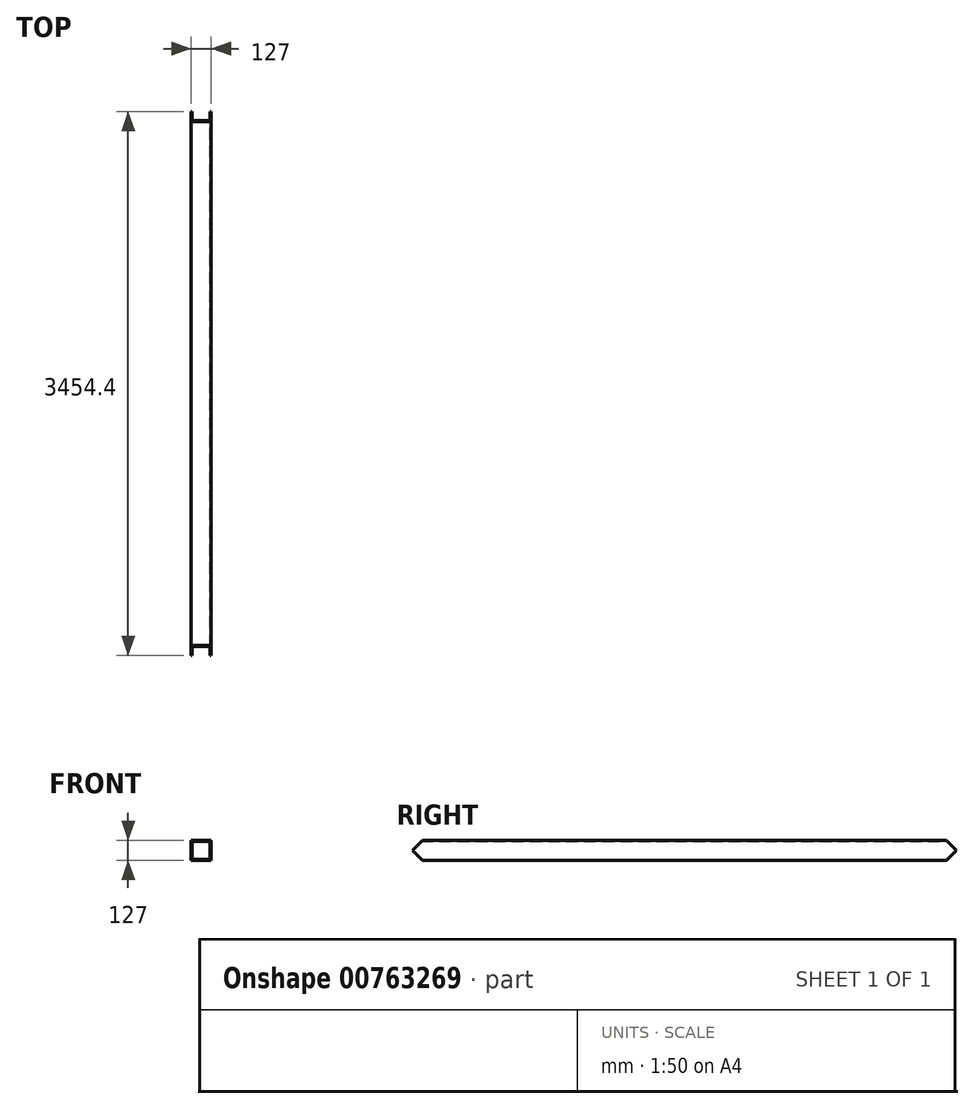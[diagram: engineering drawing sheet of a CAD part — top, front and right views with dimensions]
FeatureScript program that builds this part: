
annotation { "Feature Type Name" : "Feature", "Feature Type Description" : "" }
export const myFeature = defineFeature(function(context is Context, id is Id, definition is map)
    precondition{}
    {
        {
            var Q0;
            Q0=qCreatedBy(makeId("Front.planeOp"),FACE);
            var sketch = newSketch(context, id + "F0", { "sketchPlane" : qUnion([Q0])});
            skLineSegment(sketch, "E0.bottom", {"start": v(-63.5, 63.5) * mm, "end": v(63.5, 63.5) * mm});
            skLineSegment(sketch, "E0.top", {"start": v(-63.5, -63.5) * mm, "end": v(63.5, -63.5) * mm});
            skLineSegment(sketch, "E0.left", {"start": v(-63.5, 63.5) * mm, "end": v(-63.5, -63.5) * mm});
            skLineSegment(sketch, "E0.right", {"start": v(63.5, 63.5) * mm, "end": v(63.5, -63.5) * mm});
            skLineSegment(sketch, "E1.bottom", {"start": v(-57.15, 57.15) * mm, "end": v(57.15, 57.15) * mm});
            skLineSegment(sketch, "E1.top", {"start": v(-57.15, -57.15) * mm, "end": v(57.15, -57.15) * mm});
            skLineSegment(sketch, "E1.left", {"start": v(-57.15, 57.15) * mm, "end": v(-57.15, -57.15) * mm});
            skLineSegment(sketch, "E1.right", {"start": v(57.15, 57.15) * mm, "end": v(57.15, -57.15) * mm});
            skLineSegment(sketch, "E2", {"start": v(-57.15, 57.15) * mm, "end": v(57.15, -57.15) * mm, "construction": true});
            skLineSegment(sketch, "E3", {"start": v(63.5, 63.5) * mm, "end": v(-63.5, -63.5) * mm, "construction": true});
            skSolve(sketch);
        }
        {
            var Q0;
            Q0 = qSketchRegion(id + "F0", true);
            extrude(context, id + "F1", {"entities" : qUnion([Q0]), "endBound" : BoundingType.SYMMETRIC, "depth" : 3454.4 * mm, "offsetDistance" : 25.4 * mm});
        }
        {
            var Q0;
            Q0=makeQuery(id+"F1.opExtrude","SWEPT_FACE",FACE,{"disambiguationData":[OSD([sQuery(id+"F0.wireOp",EDGE,"E0.right")])]});
            var sketch = newSketch(context, id + "F2", { "sketchPlane" : qUnion([Q0])});
            skLineSegment(sketch, "E4", {"start": v(1727.2, 0) * mm, "end": v(1727.2, 63.5) * mm});
            skLineSegment(sketch, "E5", {"start": v(1727.2, 63.5) * mm, "end": v(1663.7, 63.5) * mm});
            skLineSegment(sketch, "E6", {"start": v(1663.7, 63.5) * mm, "end": v(1727.2, 0) * mm});
            skLineSegment(sketch, "E7", {"start": v(1727.2, 0) * mm, "end": v(1663.7, -63.5) * mm});
            skLineSegment(sketch, "E8", {"start": v(1663.7, -63.5) * mm, "end": v(1727.2, -63.5) * mm});
            skLineSegment(sketch, "E9", {"start": v(1727.2, -63.5) * mm, "end": v(1727.2, 0) * mm});
            skLineSegment(sketch, "E10", {"start": v(-1727.2, -63.5) * mm, "end": v(-1663.7, -63.5) * mm});
            skLineSegment(sketch, "E11", {"start": v(-1663.7, -63.5) * mm, "end": v(-1727.2, 0) * mm});
            skLineSegment(sketch, "E12", {"start": v(-1727.2, 0) * mm, "end": v(-1663.7, 63.5) * mm});
            skLineSegment(sketch, "E13", {"start": v(-1663.7, 63.5) * mm, "end": v(-1727.2, 63.5) * mm});
            skLineSegment(sketch, "E14", {"start": v(-1727.2, 63.5) * mm, "end": v(-1727.2, 0) * mm});
            skLineSegment(sketch, "E15", {"start": v(-1727.2, -63.5) * mm, "end": v(-1727.2, 0) * mm});
            skSolve(sketch);
        }
        {
            var Q0;
            Q0=qSketchRegion(id+"F2",true);
            extrude(context, id + "F3", {"entities" : qUnion([Q0]), "operationType" : NewBodyOperationType.REMOVE, "endBound" : BoundingType.THROUGH_ALL, "oppositeDirection" : true, "depth" : 25.4 * mm, "offsetDistance" : 25.4 * mm});
        }
    });
